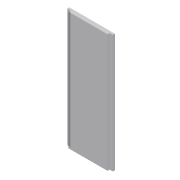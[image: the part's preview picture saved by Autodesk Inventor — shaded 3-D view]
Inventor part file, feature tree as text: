
AUTODESK INVENTOR PART (.ipt)
format: ipt  version: 2016 (Build 200138000, 138)  size: 81,408 bytes
history: native  units: mm
features: extrude x2, sketch x2
ambient origin geometry x8: Origin, YZ Plane, XZ Plane, XY Plane, X Axis, Y Axis, Z Axis, Center Point
bodies: Volumenkörper1 (feature_tree)
feature tree (4):
  extrude  "Extrusion1"  Depth=12.0mm
  extrude  "Extrusion2"  Depth=6.0mm
  sketch  "Skizze1"  dims[d0=146.0mm d1=12.0mm]
  sketch  "Skizze2"  dims[d2=289.0mm d3=0.0mm d4=6.0mm d5=128.0mm d6=64.0mm d7=300.0mm d8=0.0mm]
